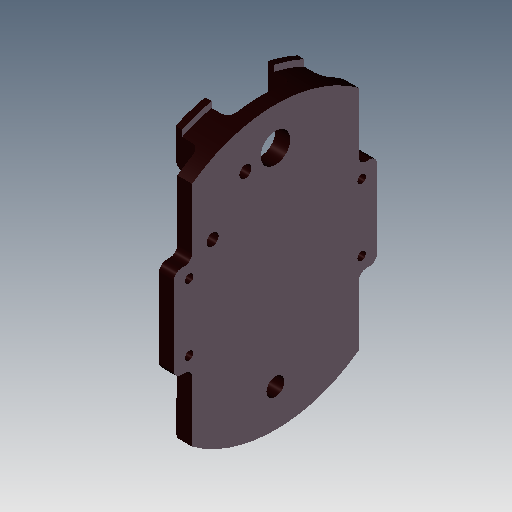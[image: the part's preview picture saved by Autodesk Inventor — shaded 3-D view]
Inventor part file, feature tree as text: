
AUTODESK INVENTOR PART (.ipt)
format: ipt  version: 2018 (Build 220112000, 112)  size: 268,288 bytes
history: native  units: mm
features: extrude x8, sketch x8, mirror x4, fillet x4
ambient origin geometry x8: Origin, YZ Plane, XZ Plane, XY Plane, X Axis, Y Axis, Z Axis, Center Point
bodies: Solid1 (feature_tree)
feature tree (24):
  extrude  "Extrusion1"  Depth=25.0mm
  extrude  "Extrusion2"  Depth=12.5mm
  mirror  "Mirror1"
  extrude  "Extrusion4"  Depth=4.0mm
  mirror  "Mirror2"
  extrude  "Extrusion6"  Depth=18.0mm
  extrude  "Extrusion7"  Depth=4.0mm
  mirror  "Mirror3"
  mirror  "Mirror4"
  fillet  "Fillet1"  Radius=4.2mm
  fillet  "Fillet2"  Radius=4.0mm
  fillet  "Fillet3"  Radius=76.2mm
  fillet  "Fillet4"  Radius=45.0mm
  extrude  "Extrusion8"  Depth=4.0mm TaperAngle=0.0deg
  extrude  "Extrusion9"  Depth=8.0mm
  extrude  "Extrusion10"  Depth=6.5mm TaperAngle=0.0deg
  sketch  "Sketch1"  dims[d0=55.0mm d1=25.0mm]
  sketch  "Sketch2"  dims[d2=27.5mm d3=12.5mm]
  sketch  "Sketch3"  dims[d4=4.0mm d5=0.0mm d6=2.3mm]
  sketch  "Sketch6"  dims[d7=2.3mm d8=18.0mm]
  sketch  "Sketch7"  dims[d9=9.0mm d10=4.2mm d11=4.2mm d12=4.0mm d13=0.0mm d14=76.2mm d15=45.0mm]
  sketch  "Sketch8"  dims[d16=22.5mm d19=4.0mm d20=0.0mm]
  sketch  "Sketch9"  dims[d29=8.0mm d30=6.0mm]
  sketch  "Sketch10"  dims[d31=8.0mm d32=6.5mm d33=0.0mm d34=79.375mm d35=1.75mm d36=0.0mm d37=2.0mm d38=2.0mm d39=2.0mm d40=2.0mm d42=3.302mm d43=15.0mm d44=17.0mm d45=3.302mm d46=8.89mm d47=11.43mm d48=10.0mm d49=0.0mm d50=4.85mm d51=27.94mm d52=10.0mm d53=0.0mm d54=6.5mm d55=10.0mm d56=0.0mm d62=8.0mm]
